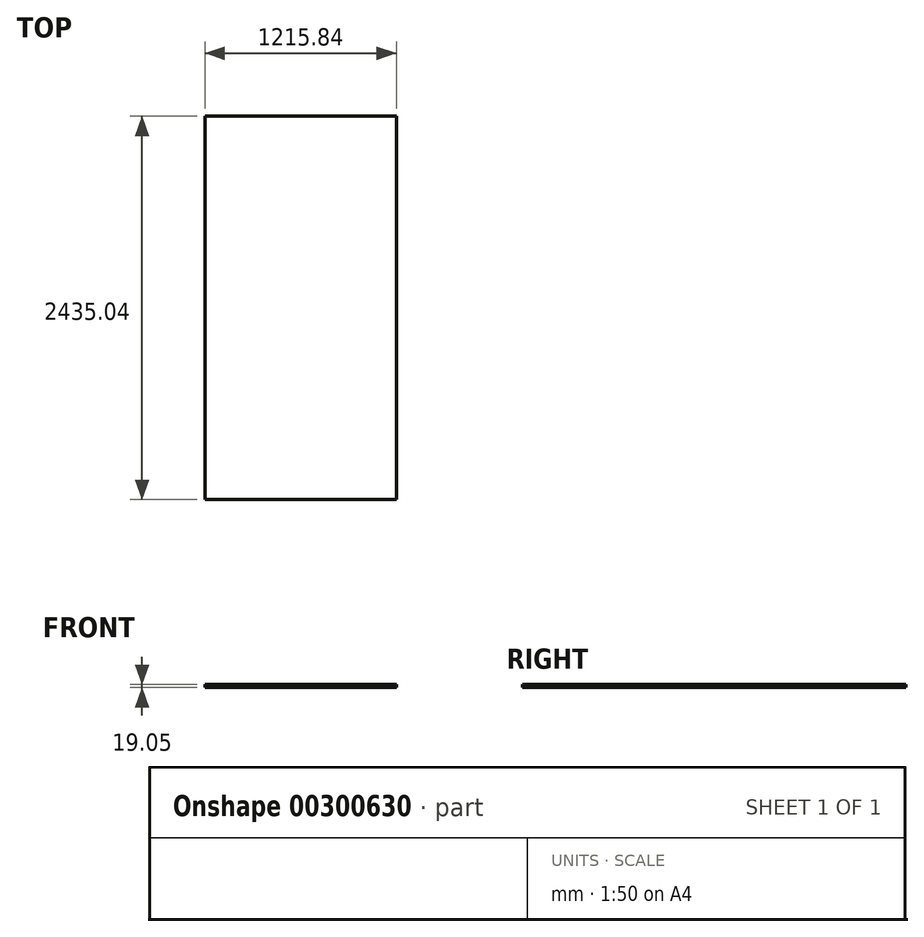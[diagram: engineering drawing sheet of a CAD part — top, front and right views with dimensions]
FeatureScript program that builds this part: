
annotation { "Feature Type Name" : "Feature", "Feature Type Description" : "" }
export const myFeature = defineFeature(function(context is Context, id is Id, definition is map)
    precondition{}
    {
        {
            var Q0;
            Q0=qCreatedBy(makeId("Top.planeOp"),FACE);
            var sketch = newSketch(context, id + "F0", { "sketchPlane" : qUnion([Q0])});
            skLineSegment(sketch, "E0.bottom", {"start": v(-607.92, -1217.52) * mm, "end": v(607.92, -1217.52) * mm});
            skLineSegment(sketch, "E0.top", {"start": v(-607.92, 1217.52) * mm, "end": v(607.92, 1217.52) * mm});
            skLineSegment(sketch, "E0.left", {"start": v(-607.92, -1217.52) * mm, "end": v(-607.92, 1217.52) * mm});
            skLineSegment(sketch, "E0.right", {"start": v(607.92, -1217.52) * mm, "end": v(607.92, 1217.52) * mm});
            skPoint(sketch, "E0.middle", {"position": v(0, 0) * mm});
            skSolve(sketch);
        }
        {
            var Q0;
            Q0 = qSketchRegion(id + "F0", true);
            extrude(context, id + "F1", {"entities" : qUnion([Q0]), "depth" : 19.05 * mm});
        }
    });
